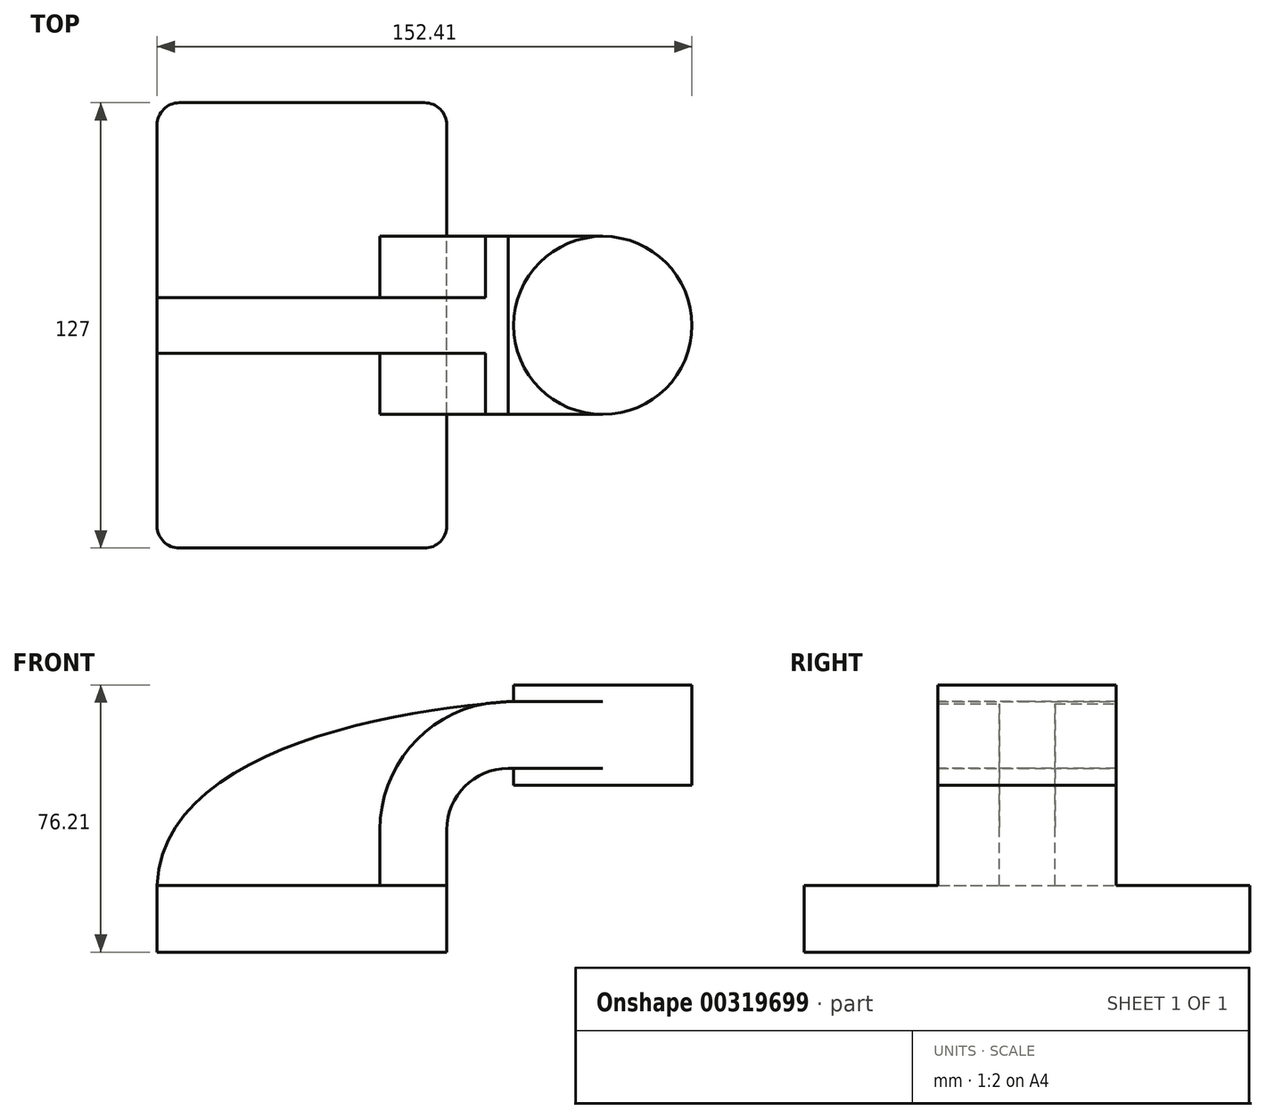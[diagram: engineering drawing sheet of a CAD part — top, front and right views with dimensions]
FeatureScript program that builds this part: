
annotation { "Feature Type Name" : "Feature", "Feature Type Description" : "" }
export const myFeature = defineFeature(function(context is Context, id is Id, definition is map)
    precondition{}
    {
        {
            var Q0;
            Q0=qCreatedBy(makeId("Front.planeOp"),FACE);
            var sketch = newSketch(context, id + "F0", { "sketchPlane" : qUnion([Q0])});
            skLineSegment(sketch, "E0.bottom", {"start": v(-41.28, -9.53) * mm, "end": v(41.28, -9.53) * mm});
            skLineSegment(sketch, "E0.top", {"start": v(-41.28, 9.53) * mm, "end": v(41.28, 9.53) * mm});
            skLineSegment(sketch, "E0.left", {"start": v(-41.28, -9.53) * mm, "end": v(-41.28, 9.53) * mm});
            skLineSegment(sketch, "E0.right", {"start": v(41.28, -9.53) * mm, "end": v(41.28, 9.53) * mm});
            skPoint(sketch, "E0.middle", {"position": v(0, 0) * mm});
            skLineSegment(sketch, "E1.bottom", {"start": v(111.12, 66.68) * mm, "end": v(60.32, 66.68) * mm});
            skLineSegment(sketch, "E1.top", {"start": v(111.12, 38.1) * mm, "end": v(60.33, 38.1) * mm});
            skLineSegment(sketch, "E1.left", {"start": v(111.12, 66.67) * mm, "end": v(111.12, 38.1) * mm});
            skLineSegment(sketch, "E1.right", {"start": v(60.32, 66.67) * mm, "end": v(60.33, 38.1) * mm});
            skPoint(sketch, "E1.middle", {"position": v(85.72, 52.39) * mm});
            skLineSegment(sketch, "E2", {"start": v(41.28, 9.52) * mm, "end": v(41.28, 25.37) * mm});
            skArc(sketch, "E3", {"start": v(41.27, 25.37) * mm, "mid": v(46.4, 37.74) * mm, "end": v(58.77, 42.86) * mm});
            skLineSegment(sketch, "E4", {"start": v(58.77, 42.86) * mm, "end": v(85.72, 42.86) * mm});
            skLineSegment(sketch, "E5.0", {"start": v(58.77, 61.91) * mm, "end": v(85.72, 61.91) * mm});
            skArc(sketch, "E5.1", {"start": v(22.22, 25.37) * mm, "mid": v(32.93, 51.2) * mm, "end": v(58.77, 61.91) * mm});
            skLineSegment(sketch, "E5.2", {"start": v(22.22, 9.52) * mm, "end": v(22.22, 25.37) * mm});
            skLineSegment(sketch, "E6", {"start": v(85.72, 38.1) * mm, "end": v(85.72, 66.68) * mm});
            skPoint(sketch, "E7.1.internal.snap0", {"position": v(32.93, 51.2) * mm});
            skFitSpline(sketch, "E8", {"points": [v(-41.28, 9.53) * mm, v(58.77, 61.91) * mm], "startDerivative": vector(4.35, 112.66) * mm, "endDerivative": vector(111.74, 8.8) * mm});
            skSolve(sketch);
        }
        {
            var Q0;
            Q0=makeQuery(id+"F0.imprint","IMPRINT",FACE,{"disambiguationData":[TD([[makeQuery(id+"F0.imprint","IMPRINT",EDGE,{"derivedFrom":sQuery(id+"F0.wireOp",EDGE,"E0.bottom")}),1.0]])]});
            extrude(context, id + "F1", {"entities" : qUnion([Q0]), "endBound" : BoundingType.SYMMETRIC, "depth" : 127 * mm});
        }
        {
            var Q0;
            {var subQ1=sQuery(id+"F0.wireOp",EDGE,"E2");Q0=makeQuery(id+"F0.imprint","IMPRINT",FACE,{"disambiguationData":[TD([[makeQuery(id+"F0.imprint","IMPRINT",EDGE,{"derivedFrom":subQ1}),1.0]])]});}
            var Q1;
            {var subQ0=sQuery(id+"F0.wireOp",EDGE,"E5.0");var subQ1=sQuery(id+"F0.wireOp",EDGE,"E1.right");var subQ2=makeQuery(id+"F0.imprint","INTERSECT",VERTEX,{"derivedFrom":[subQ1,subQ0]});Q1=makeQuery(id+"F0.imprint","IMPRINT",FACE,{"disambiguationData":[TD([[makeQuery(id+"F0.imprint","IMPRINT",EDGE,{"disambiguationData":[TD([[subQ2,-1.0]])],"derivedFrom":subQ1}),1.0]])]});}
            extrude(context, id + "F2", {"entities" : qUnion([Q0, Q1]), "operationType" : NewBodyOperationType.ADD, "endBound" : BoundingType.SYMMETRIC, "depth" : 50.8 * mm});
        }
        {
            var Q0;
            {var subQ3=sQuery(id+"F0.wireOp",EDGE,"E5.2");Q0=makeQuery(id+"F0.imprint","IMPRINT",FACE,{"disambiguationData":[TD([[makeQuery(id+"F0.imprint","IMPRINT",EDGE,{"derivedFrom":subQ3}),1.0]])]});}
            extrude(context, id + "F3", {"entities" : qUnion([Q0]), "operationType" : NewBodyOperationType.ADD, "endBound" : BoundingType.SYMMETRIC, "depth" : 15.88 * mm});
        }
        {
            var Q0;
            {var subQ0=sQuery(id+"F0.wireOp",EDGE,"E1.left");Q0=makeQuery(id+"F0.imprint","IMPRINT",FACE,{"disambiguationData":[TD([[makeQuery(id+"F0.imprint","IMPRINT",EDGE,{"derivedFrom":subQ0}),-1.0]])]});}
            var Q1;
            Q1=sQuery(id+"F0.wireOp",EDGE,"E6");
            revolve(context, id + "F4", {"operationType" : NewBodyOperationType.ADD, "entities" : qUnion([Q0]), "axis" : qUnion([Q1]), "revolveType" : RevolveType.FULL});
        }
        {
            var Q0;
            Q0=makeQuery(id+"F1.opExtrude","CAP_EDGE",EDGE,{"disambiguationData":[OSD([sQuery(id+"F0.wireOp",EDGE,"E0.left")])],"isStart":false});
            var Q1;
            Q1=makeQuery(id+"F1.opExtrude","CAP_EDGE",EDGE,{"disambiguationData":[OSD([sQuery(id+"F0.wireOp",EDGE,"E0.right")])],"isStart":false});
            var Q2;
            Q2=makeQuery(id+"F1.opExtrude","CAP_EDGE",EDGE,{"disambiguationData":[OSD([sQuery(id+"F0.wireOp",EDGE,"E0.right")])],"isStart":true});
            var Q3;
            Q3=makeQuery(id+"F1.opExtrude","CAP_EDGE",EDGE,{"disambiguationData":[OSD([sQuery(id+"F0.wireOp",EDGE,"E0.left")])],"isStart":true});
            fillet(context, id + "F5", {"entities" : qUnion([Q0, Q1, Q2, Q3]), "radius" : 6.35 * mm, "tangentPropagation" : true, "allowEdgeOverflow" : false});
        }
    });
